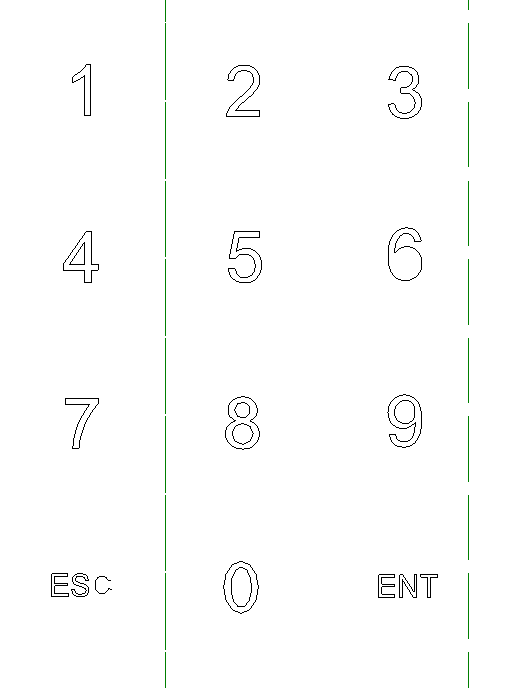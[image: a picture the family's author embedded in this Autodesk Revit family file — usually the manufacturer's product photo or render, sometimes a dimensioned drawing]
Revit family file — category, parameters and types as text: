
# Revit family: STS-708M_RV17_LOD_400
name_source: partatom
category: Электрооборудование
revit_build: Autodesk Revit 2017 (Build: 20170118_1100(x64)
units: mm (PartAtom-declared; Revit-internal decimal feet)

## family parameters
Всегда вертикально = Да
Конфигурация панели = Два столбца, слева направо
На основе рабочей плоскости = Нет
Общий = Нет
При загрузке вырезать с полостями = Нет
Размер круглого соединителя = Использовать диаметр
Тип детали = Щит
Точка расчета площади = Нет

## types (1)
- STS-708M
    ADSK_URL страницы изделия = https://stilsoft.ru
    ADSK_Единица измерения = шт.
    ADSK_Завод-изготовитель = ООО «Основа Безопасности»
    ADSK_Количество = 1
    ADSK_Марка = СТВФ.431295.148
    ADSK_Масса = 0.25
    ADSK_Наименование = STS-708M
    ADSK_Размер_Высота = 108 мм
    ADSK_Размер_Глубина = 35 мм
    ADSK_Размер_Ширина = 87 мм
    Антенна = встроенная
    Время считывания проксимити-карт, не более, мс = 200
    Диапазон рабочих температур, °С = от минус 40 до плюс 50
    Идентификаторы = MIFARE Classic 1K
    Идентификаторы (2) = MIFARE Classic 4K
    Идентификаторы (3) = MIFARE Classic Mini
    Идентификаторы (4) = MIFARE Ultralight
    Идентификаторы (5) = MIFARE Ultralight C
    Информационные интерфейсы = RS-485
    Напряжение = 12
    Номинальная дальность считывания = 1-7 (зависит от
идентификатора доступа)
    Потребляемый ток, не более, А = 0.08
    Тип идентификаторов = карта, брелок
    Частота, кГц = 13.56
